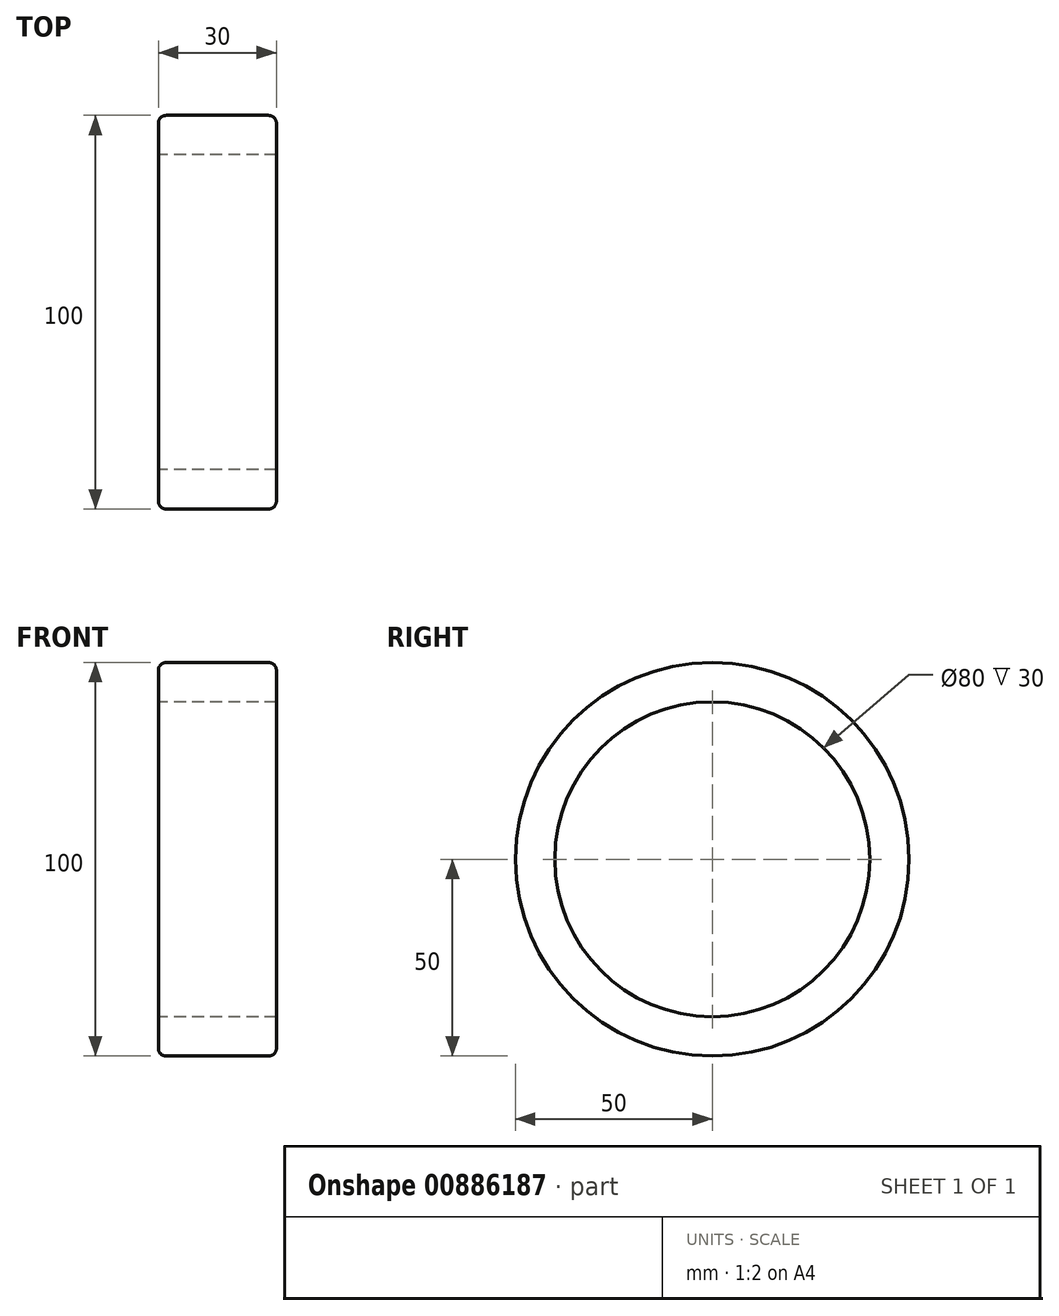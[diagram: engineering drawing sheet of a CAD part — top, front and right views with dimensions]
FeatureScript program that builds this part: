
annotation { "Feature Type Name" : "Feature", "Feature Type Description" : "" }
export const myFeature = defineFeature(function(context is Context, id is Id, definition is map)
    precondition{}
    {
        {
            var Q0;
            Q0=qCreatedBy(makeId("Right.planeOp"),FACE);
            var sketch = newSketch(context, id + "F0", { "sketchPlane" : qUnion([Q0])});
            skCircle(sketch, "E0", {"center": v(0, 0) * mm, "radius": 50 * mm});
            skCircle(sketch, "E1", {"center": v(0, 0) * mm, "radius": 8 * mm});
            skCircle(sketch, "E2", {"center": v(0, 0) * mm, "radius": 40 * mm});
            skSolve(sketch);
        }
        {
            var Q0;
            Q0=makeQuery(id+"F0.imprint","IMPRINT",FACE,{"disambiguationData":[TD([[makeQuery(id+"F0.imprint","IMPRINT",EDGE,{"derivedFrom":sQuery(id+"F0.wireOp",EDGE,"E0")}),1.0]])]});
            extrude(context, id + "F1", {"entities" : qUnion([Q0]), "depth" : 28 * mm, "offsetDistance" : 25 * mm});
        }
        {
            var Q0;
            Q0 = qSketchRegion(id + "F0", true);
            extrude(context, id + "F2", {"entities" : qUnion([Q0]), "operationType" : NewBodyOperationType.ADD, "depth" : 30 * mm, "offsetDistance" : 25 * mm});
        }
        {
            var Q0;
            Q0=makeQuery(id+"F2.opExtrude","CAP_EDGE",EDGE,{"disambiguationData":[OSD([sQuery(id+"F0.wireOp",EDGE,"E0")])],"isStart":false});
            fillet(context, id + "F3", {"entities" : qUnion([Q0]), "radius" : 2 * mm, "tangentPropagation" : true, "allowEdgeOverflow" : false});
        }
        {
            var Q0;
            Q0=makeQuery(id+"F1.opExtrude","CAP_EDGE",EDGE,{"disambiguationData":[OSD([sQuery(id+"F0.wireOp",EDGE,"E0")])],"isStart":true});
            fillet(context, id + "F4", {"entities" : qUnion([Q0]), "radius" : 2 * mm, "tangentPropagation" : true, "allowEdgeOverflow" : false});
        }
    });
